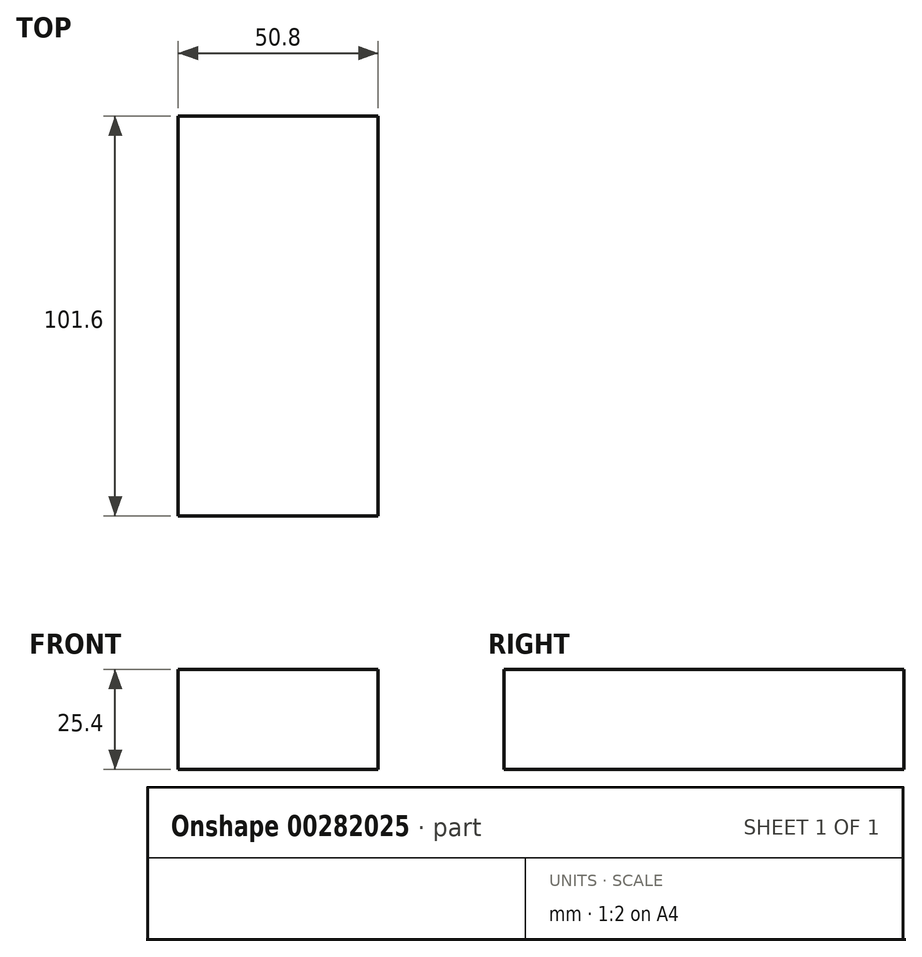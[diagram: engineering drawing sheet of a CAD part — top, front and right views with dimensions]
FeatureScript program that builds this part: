
annotation { "Feature Type Name" : "Feature", "Feature Type Description" : "" }
export const myFeature = defineFeature(function(context is Context, id is Id, definition is map)
    precondition{}
    {
        {
            var Q0;
            Q0=qCreatedBy(makeId("Top.planeOp"),FACE);
            var sketch = newSketch(context, id + "F0", { "sketchPlane" : qUnion([Q0])});
            skLineSegment(sketch, "E0.bottom", {"start": v(50.8, 101.6) * mm, "end": v(0, 101.6) * mm});
            skLineSegment(sketch, "E0.top", {"start": v(50.8, 0) * mm, "end": v(0, 0) * mm});
            skLineSegment(sketch, "E0.left", {"start": v(50.8, 101.6) * mm, "end": v(50.8, 0) * mm});
            skLineSegment(sketch, "E0.right", {"start": v(0, 101.6) * mm, "end": v(0, 0) * mm});
            skSolve(sketch);
        }
        {
            var Q0;
            Q0 = qSketchRegion(id + "F0", true);
            extrude(context, id + "F1", {"entities" : qUnion([Q0]), "endBound" : BoundingType.SYMMETRIC, "depth" : 25.4 * mm});
        }
    });
